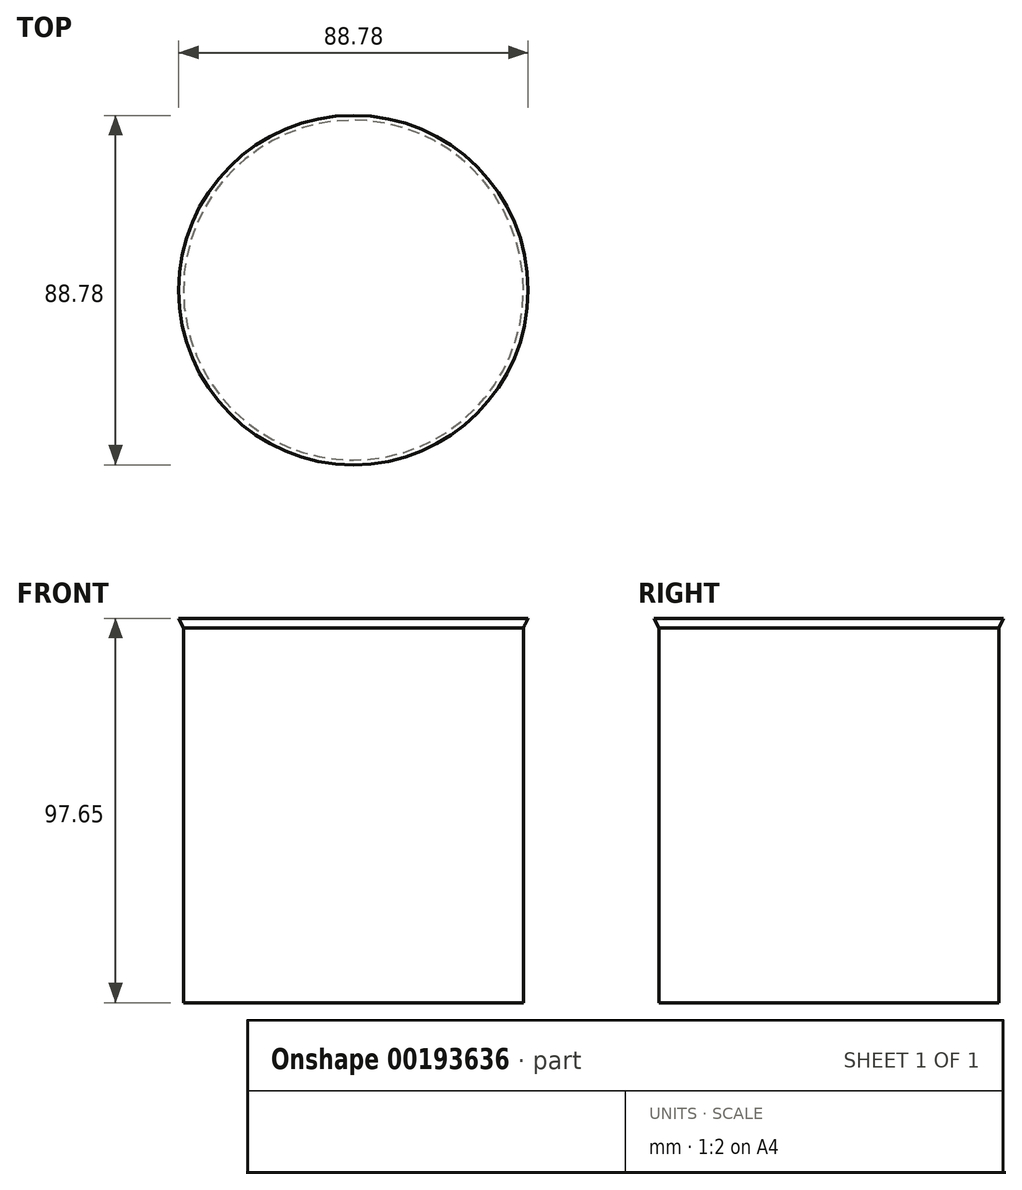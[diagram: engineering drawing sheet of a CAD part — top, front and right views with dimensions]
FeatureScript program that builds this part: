
annotation { "Feature Type Name" : "Feature", "Feature Type Description" : "" }
export const myFeature = defineFeature(function(context is Context, id is Id, definition is map)
    precondition{}
    {
        {
            var Q0;
            Q0=qCreatedBy(makeId("Front.planeOp"),FACE);
            var sketch = newSketch(context, id + "F0", { "sketchPlane" : qUnion([Q0])});
            skLineSegment(sketch, "E0", {"start": v(0, 57.9) * mm, "end": v(0, -52.46) * mm});
            skLineSegment(sketch, "E1", {"start": v(0, -52.46) * mm, "end": v(43.18, -52.46) * mm});
            skLineSegment(sketch, "E2", {"start": v(43.18, -52.46) * mm, "end": v(43.18, 42.8) * mm});
            skLineSegment(sketch, "E3", {"start": v(0, 57.9) * mm, "end": v(50.8, 57.9) * mm});
            skLineSegment(sketch, "E4", {"start": v(50.8, 57.9) * mm, "end": v(43.18, 42.8) * mm});
            skSolve(sketch);
        }
        {
            var Q0;
            Q0 = qSketchRegion(id + "F0", true);
            var Q1;
            Q1=sQuery(id+"F0.wireOp",EDGE,"E0");
            revolve(context, id + "F1", {"entities" : qUnion([Q0]), "axis" : qUnion([Q1]), "revolveType" : RevolveType.FULL});
        }
        {
            var Q0;
            Q0=makeQuery(id+"F1.opRevolve","SWEPT_FACE",FACE,{"disambiguationData":[OSD([sQuery(id+"F0.wireOp",EDGE,"E3")])]});
            extrude(context, id + "F2", {"entities" : qUnion([Q0]), "operationType" : NewBodyOperationType.REMOVE, "oppositeDirection" : true, "depth" : 12.7 * mm});
        }
    });
